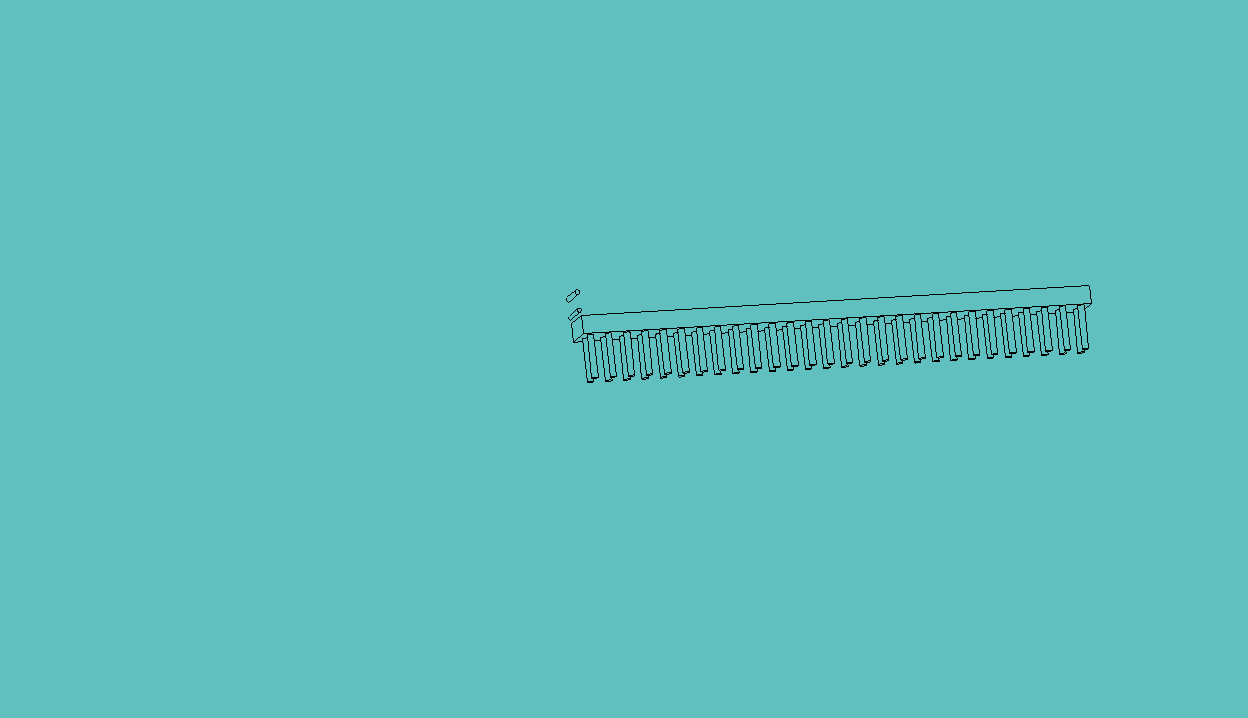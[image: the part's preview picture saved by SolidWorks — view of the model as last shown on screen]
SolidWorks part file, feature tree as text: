
SOLIDWORKS PART (.sldprt)
format: sldprt  version: not decoded by parser v0  size: 177,664 bytes
history: native  units: mm
features: sketch x3, extrude x3, material x1, pattern_linear x1 (+12 scaffold rows collapsed)
feature tree (20):
  scaffold x12  (default folders/planes/origin — collapsed)
  material  "Material <not specified>"
  sketch  "Sketch1"  dims[D1=2.54mm D2=5.461mm]
  extrude  "Extrude1"  Depth=2.54mm
  sketch  "Sketch2"  dims[D5=0.889mm D6=0.889mm D1=1.905mm D2=1.27mm D3=1.27mm D4=2.54mm]
  extrude  "Extrude2"  Depth=5.969mm
  sketch  "Sketch3"  dims[D1=2.54mm D2=1.778mm D3=1.27mm]
  extrude  "Extrude3"  Depth=5.08mm
  pattern_linear  "LPattern1"  Count1=28 Count2=1 Spacing1=2.54mm Spacing2=50mm
decode coverage: 7 of 7 modeling features carry decoded parameters
note: suppression state not decoded; provenance and decode notes live in map.json
